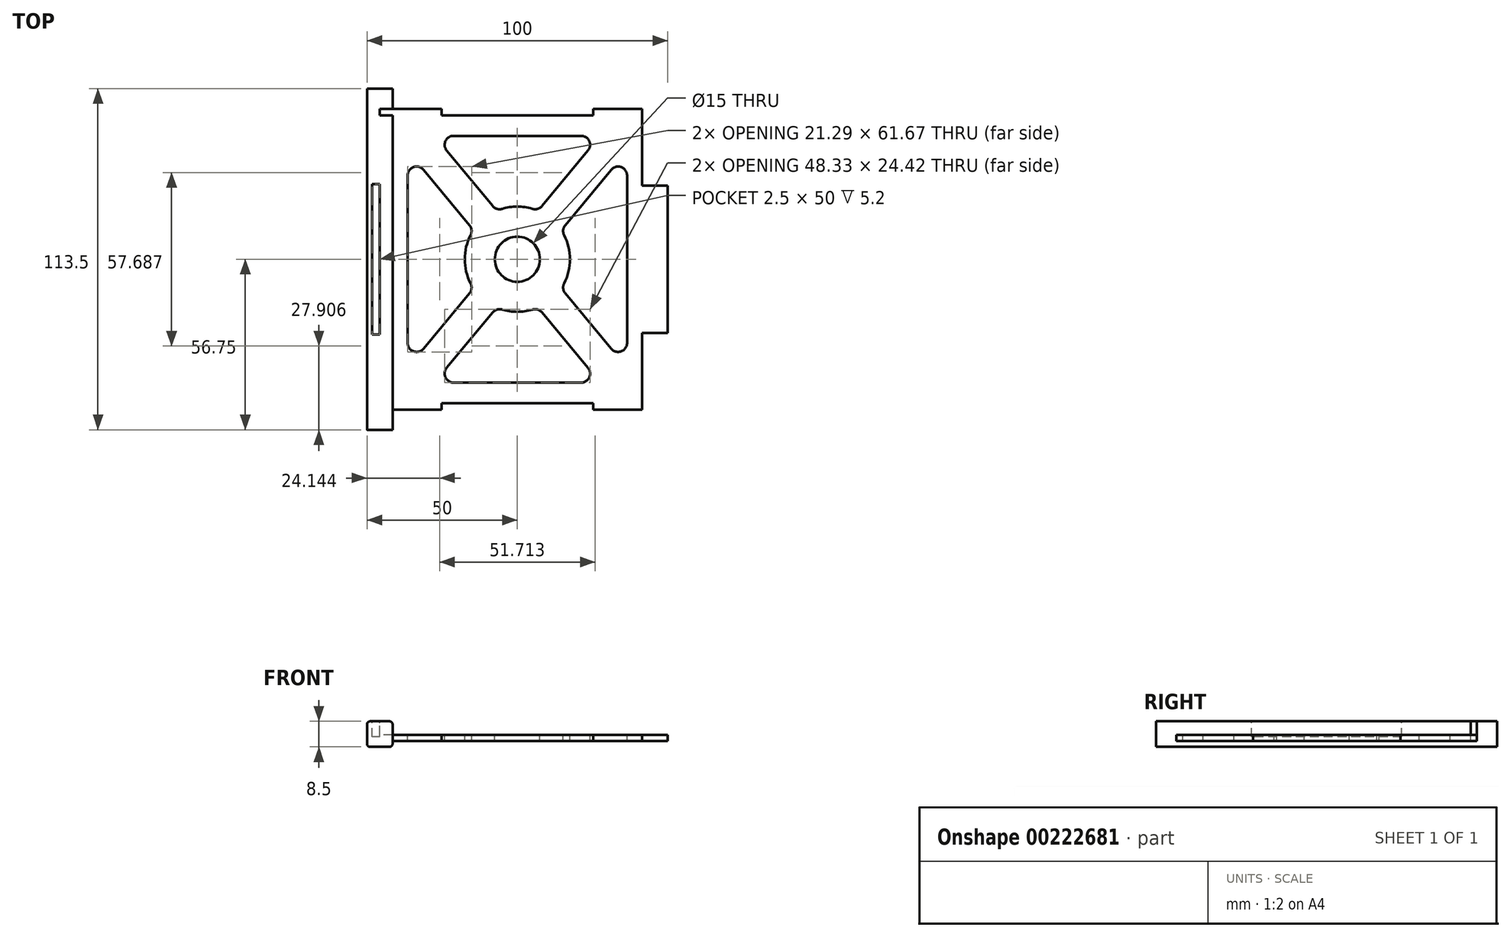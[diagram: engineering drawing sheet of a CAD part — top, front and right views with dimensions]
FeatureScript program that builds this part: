
annotation { "Feature Type Name" : "Feature", "Feature Type Description" : "" }
export const myFeature = defineFeature(function(context is Context, id is Id, definition is map)
    precondition{}
    {
        {
            var Q0;
            Q0=qCreatedBy(makeId("Top.planeOp"),FACE);
            var sketch = newSketch(context, id + "F0", { "sketchPlane" : qUnion([Q0])});
            skLineSegment(sketch, "E0.bottom", {"start": v(-50, 50) * mm, "end": v(50, 50) * mm});
            skLineSegment(sketch, "E0.top", {"start": v(-50, -50) * mm, "end": v(50, -50) * mm});
            skLineSegment(sketch, "E0.left", {"start": v(-50, 50) * mm, "end": v(-50, -50) * mm});
            skLineSegment(sketch, "E0.right", {"start": v(50, 50) * mm, "end": v(50, -50) * mm});
            skPoint(sketch, "E0.middle", {"position": v(0, 0) * mm});
            skSolve(sketch);
        }
        {
            var Q0;
            Q0=makeQuery(id+"F0.imprint","IMPRINT",FACE,{"disambiguationData":[TD([[makeQuery(id+"F0.imprint","IMPRINT",EDGE,{"derivedFrom":sQuery(id+"F0.wireOp",EDGE,"E0.bottom")}),-1.0]])]});
            extrude(context, id + "F1", {"entities" : qUnion([Q0]), "depth" : 2 * mm});
        }
        {
            var Q0;
            Q0=makeQuery(id+"F1.opExtrude","CAP_FACE",FACE,{"disambiguationData":[OSD([sQuery(id+"F0.wireOp",EDGE,"E0.bottom"),sQuery(id+"F0.wireOp",EDGE,"E0.top"),sQuery(id+"F0.wireOp",EDGE,"E0.left"),sQuery(id+"F0.wireOp",EDGE,"E0.right")])],"isStart":false});
            var sketch = newSketch(context, id + "F2", { "sketchPlane" : qUnion([Q0])});
            skCircle(sketch, "E1", {"center": v(0, 0) * mm, "radius": 7.5 * mm});
            skArc(sketch, "E2", {"start": v(-15.55, 8.04) * mm, "mid": v(-17.5, 0) * mm, "end": v(-15.55, -8.04) * mm});
            skLineSegment(sketch, "E3", {"start": v(41.5, 50) * mm, "end": v(0, 0) * mm, "construction": true});
            skLineSegment(sketch, "E4", {"start": v(-41.5, 50) * mm, "end": v(0, 0) * mm, "construction": true});
            skLineSegment(sketch, "E5", {"start": v(0, 0) * mm, "end": v(-41.5, -50) * mm, "construction": true});
            skLineSegment(sketch, "E6", {"start": v(0, 0) * mm, "end": v(41.5, -50) * mm, "construction": true});
            skLineSegment(sketch, "E7", {"start": v(-23.5, 36.14) * mm, "end": v(-8.2, 17.72) * mm});
            skLineSegment(sketch, "E8", {"start": v(-31.2, 29.75) * mm, "end": v(-15.9, 11.33) * mm});
            skLineSegment(sketch, "E9", {"start": v(-36.5, 27.84) * mm, "end": v(-36.5, -27.84) * mm});
            skLineSegment(sketch, "E10", {"start": v(-31.2, -29.75) * mm, "end": v(-15.9, -11.33) * mm});
            skLineSegment(sketch, "E11", {"start": v(-21.19, 41.05) * mm, "end": v(21.19, 41.05) * mm});
            skLineSegment(sketch, "E12", {"start": v(23.5, 36.14) * mm, "end": v(8.2, 17.72) * mm});
            skLineSegment(sketch, "E13", {"start": v(0, 50) * mm, "end": v(0, -50) * mm, "construction": true});
            skLineSegment(sketch, "E14", {"start": v(-41.5, 0) * mm, "end": v(41.5, 0) * mm, "construction": true});
            skLineSegment(sketch, "E15.MirrorCS", {"start": v(31.2, -29.75) * mm, "end": v(15.9, -11.33) * mm});
            skLineSegment(sketch, "E16.MirrorCS", {"start": v(31.2, 29.75) * mm, "end": v(15.9, 11.33) * mm});
            skLineSegment(sketch, "E17.MirrorCS", {"start": v(36.5, 27.84) * mm, "end": v(36.5, -27.84) * mm});
            skLineSegment(sketch, "E18.MirrorCS", {"start": v(23.5, -36.14) * mm, "end": v(8.2, -17.72) * mm});
            skLineSegment(sketch, "E19.MirrorCS", {"start": v(-23.5, -36.14) * mm, "end": v(-8.2, -17.72) * mm});
            skLineSegment(sketch, "E20.MirrorCS", {"start": v(-21.19, -41.05) * mm, "end": v(21.19, -41.05) * mm});
            skArc(sketch, "E21.trimOffspring", {"start": v(5.04, 16.76) * mm, "mid": v(0, 17.5) * mm, "end": v(-5.04, 16.76) * mm});
            skArc(sketch, "E22.trimOffspring", {"start": v(15.55, -8.04) * mm, "mid": v(17.5, 0) * mm, "end": v(15.55, 8.04) * mm});
            skArc(sketch, "E23.trimOffspring", {"start": v(-5.04, -16.76) * mm, "mid": v(0, -17.5) * mm, "end": v(5.04, -16.76) * mm});
            skPoint(sketch, "E24.visualSharp", {"position": v(-27.58, 41.05) * mm});
            skArc(sketch, "E24.filletArc", {"start": v(-21.19, 41.05) * mm, "mid": v(-23.9, 39.33) * mm, "end": v(-23.5, 36.14) * mm});
            skPoint(sketch, "E25.visualSharp", {"position": v(27.58, 41.05) * mm});
            skArc(sketch, "E25.filletArc", {"start": v(23.5, 36.14) * mm, "mid": v(23.9, 39.33) * mm, "end": v(21.19, 41.05) * mm});
            skPoint(sketch, "E26.visualSharp", {"position": v(6.86, 16.1) * mm});
            skArc(sketch, "E26.filletArc", {"start": v(5.04, 16.76) * mm, "mid": v(6.77, 16.76) * mm, "end": v(8.2, 17.72) * mm});
            skPoint(sketch, "E27.visualSharp", {"position": v(-6.86, 16.1) * mm});
            skArc(sketch, "E27.filletArc", {"start": v(-8.2, 17.72) * mm, "mid": v(-6.77, 16.76) * mm, "end": v(-5.04, 16.76) * mm});
            skPoint(sketch, "E28.visualSharp", {"position": v(-14.56, 9.71) * mm});
            skArc(sketch, "E28.filletArc", {"start": v(-15.55, 8.04) * mm, "mid": v(-15.23, 9.74) * mm, "end": v(-15.9, 11.33) * mm});
            skPoint(sketch, "E29.visualSharp", {"position": v(-36.5, 36.15) * mm});
            skArc(sketch, "E29.filletArc", {"start": v(-31.2, 29.75) * mm, "mid": v(-34.52, 30.66) * mm, "end": v(-36.5, 27.84) * mm});
            skPoint(sketch, "E30.visualSharp", {"position": v(-36.5, -36.15) * mm});
            skArc(sketch, "E30.filletArc", {"start": v(-36.5, -27.84) * mm, "mid": v(-34.52, -30.66) * mm, "end": v(-31.2, -29.75) * mm});
            skPoint(sketch, "E31.visualSharp", {"position": v(-14.56, -9.71) * mm});
            skArc(sketch, "E31.filletArc", {"start": v(-15.9, -11.33) * mm, "mid": v(-15.23, -9.74) * mm, "end": v(-15.55, -8.04) * mm});
            skPoint(sketch, "E32.visualSharp", {"position": v(14.56, 9.71) * mm});
            skArc(sketch, "E32.filletArc", {"start": v(15.9, 11.33) * mm, "mid": v(15.23, 9.74) * mm, "end": v(15.55, 8.04) * mm});
            skPoint(sketch, "E33.visualSharp", {"position": v(14.56, -9.71) * mm});
            skArc(sketch, "E33.filletArc", {"start": v(15.55, -8.04) * mm, "mid": v(15.23, -9.74) * mm, "end": v(15.9, -11.33) * mm});
            skPoint(sketch, "E34.visualSharp", {"position": v(6.86, -16.1) * mm});
            skArc(sketch, "E34.filletArc", {"start": v(8.2, -17.72) * mm, "mid": v(6.77, -16.76) * mm, "end": v(5.04, -16.76) * mm});
            skPoint(sketch, "E35.visualSharp", {"position": v(-6.86, -16.1) * mm});
            skArc(sketch, "E35.filletArc", {"start": v(-5.04, -16.76) * mm, "mid": v(-6.77, -16.76) * mm, "end": v(-8.2, -17.72) * mm});
            skPoint(sketch, "E36.visualSharp", {"position": v(-27.58, -41.05) * mm});
            skArc(sketch, "E36.filletArc", {"start": v(-23.5, -36.14) * mm, "mid": v(-23.9, -39.33) * mm, "end": v(-21.19, -41.05) * mm});
            skPoint(sketch, "E37.visualSharp", {"position": v(27.58, -41.05) * mm});
            skArc(sketch, "E37.filletArc", {"start": v(21.19, -41.05) * mm, "mid": v(23.9, -39.33) * mm, "end": v(23.5, -36.14) * mm});
            skPoint(sketch, "E38.visualSharp", {"position": v(36.5, -36.15) * mm});
            skArc(sketch, "E38.filletArc", {"start": v(31.2, -29.75) * mm, "mid": v(34.52, -30.66) * mm, "end": v(36.5, -27.84) * mm});
            skPoint(sketch, "E39.visualSharp", {"position": v(36.5, 36.15) * mm});
            skArc(sketch, "E39.filletArc", {"start": v(36.5, 27.84) * mm, "mid": v(34.52, 30.66) * mm, "end": v(31.2, 29.75) * mm});
            skLineSegment(sketch, "E40", {"start": v(41.5, 50) * mm, "end": v(41.5, -50) * mm, "construction": true});
            skLineSegment(sketch, "E41", {"start": v(-41.5, -50) * mm, "end": v(-41.5, 50) * mm, "construction": true});
            skLineSegment(sketch, "E42.bottom", {"start": v(-25.25, 50) * mm, "end": v(25.25, 50) * mm});
            skLineSegment(sketch, "E42.top", {"start": v(-25.25, 47.9) * mm, "end": v(25.25, 47.9) * mm});
            skLineSegment(sketch, "E42.left", {"start": v(-25.25, 50) * mm, "end": v(-25.25, 47.9) * mm});
            skLineSegment(sketch, "E42.right", {"start": v(25.25, 50) * mm, "end": v(25.25, 47.9) * mm});
            skLineSegment(sketch, "E43.MirrorCS", {"start": v(25.25, -50) * mm, "end": v(25.25, -47.9) * mm});
            skLineSegment(sketch, "E44.MirrorCS", {"start": v(-25.25, -50) * mm, "end": v(-25.25, -47.9) * mm});
            skLineSegment(sketch, "E45.MirrorCS", {"start": v(-25.25, -50) * mm, "end": v(25.25, -50) * mm});
            skLineSegment(sketch, "E46.MirrorCS", {"start": v(-25.25, -47.9) * mm, "end": v(25.25, -47.9) * mm});
            skSolve(sketch);
        }
        {
            var Q0;
            Q0=makeQuery(id+"F2.imprint","IMPRINT",FACE,{"disambiguationData":[TD([[makeQuery(id+"F2.imprint","IMPRINT",EDGE,{"derivedFrom":sQuery(id+"F2.wireOp",EDGE,"E7")}),1.0]])]});
            var Q1;
            Q1=makeQuery(id+"F2.imprint","IMPRINT",FACE,{"disambiguationData":[TD([[makeQuery(id+"F2.imprint","IMPRINT",EDGE,{"derivedFrom":sQuery(id+"F2.wireOp",EDGE,"E2")}),-1.0]])]});
            var Q2;
            Q2=makeQuery(id+"F2.imprint","IMPRINT",FACE,{"disambiguationData":[TD([[makeQuery(id+"F2.imprint","IMPRINT",EDGE,{"derivedFrom":sQuery(id+"F2.wireOp",EDGE,"E1")}),1.0]])]});
            var Q3;
            Q3=makeQuery(id+"F2.imprint","IMPRINT",FACE,{"disambiguationData":[TD([[makeQuery(id+"F2.imprint","IMPRINT",EDGE,{"derivedFrom":sQuery(id+"F2.wireOp",EDGE,"E15.MirrorCS")}),-1.0]])]});
            var Q4;
            Q4=makeQuery(id+"F2.imprint","IMPRINT",FACE,{"disambiguationData":[TD([[makeQuery(id+"F2.imprint","IMPRINT",EDGE,{"derivedFrom":sQuery(id+"F2.wireOp",EDGE,"E18.MirrorCS")}),1.0]])]});
            var Q5;
            Q5=makeQuery(id+"F2.imprint","IMPRINT",FACE,{"disambiguationData":[TD([[makeQuery(id+"F2.imprint","IMPRINT",EDGE,{"derivedFrom":sQuery(id+"F2.wireOp",EDGE,"E42.bottom")}),-1.0]])]});
            var Q6;
            Q6=makeQuery(id+"F2.imprint","IMPRINT",FACE,{"disambiguationData":[TD([[makeQuery(id+"F2.imprint","IMPRINT",EDGE,{"derivedFrom":sQuery(id+"F2.wireOp",EDGE,"E43.MirrorCS")}),1.0]])]});
            extrude(context, id + "F3", {"entities" : qUnion([Q0, Q1, Q2, Q3, Q4, Q5, Q6]), "operationType" : NewBodyOperationType.REMOVE, "oppositeDirection" : true, "depth" : 25 * mm});
        }
        {
            var Q0;
            Q0=makeQuery(id+"F1.opExtrude","CAP_FACE",FACE,{"disambiguationData":[OSD([sQuery(id+"F0.wireOp",EDGE,"E0.bottom"),sQuery(id+"F0.wireOp",EDGE,"E0.top"),sQuery(id+"F0.wireOp",EDGE,"E0.left"),sQuery(id+"F0.wireOp",EDGE,"E0.right")])],"isStart":true});
            var sketch = newSketch(context, id + "F4", { "sketchPlane" : qUnion([Q0])});
            skLineSegment(sketch, "E47.bottom", {"start": v(-50, 50) * mm, "end": v(-41.5, 50) * mm});
            skLineSegment(sketch, "E47.top", {"start": v(-50, -50) * mm, "end": v(-41.5, -50) * mm});
            skLineSegment(sketch, "E47.left", {"start": v(-50, 50) * mm, "end": v(-50, -50) * mm});
            skLineSegment(sketch, "E47.right", {"start": v(-41.5, 50) * mm, "end": v(-41.5, -50) * mm});
            skLineSegment(sketch, "E48.bottom", {"start": v(50, 50) * mm, "end": v(41.5, 50) * mm});
            skLineSegment(sketch, "E48.top", {"start": v(50, 24.5) * mm, "end": v(41.5, 24.5) * mm});
            skLineSegment(sketch, "E48.left", {"start": v(50, 50) * mm, "end": v(50, 24.5) * mm});
            skLineSegment(sketch, "E48.right", {"start": v(41.5, 50) * mm, "end": v(41.5, 24.5) * mm});
            skLineSegment(sketch, "E49.bottom", {"start": v(50, -50) * mm, "end": v(41.5, -50) * mm});
            skLineSegment(sketch, "E49.top", {"start": v(50, -24.5) * mm, "end": v(41.5, -24.5) * mm});
            skLineSegment(sketch, "E49.left", {"start": v(50, -50) * mm, "end": v(50, -24.5) * mm});
            skLineSegment(sketch, "E49.right", {"start": v(41.5, -50) * mm, "end": v(41.5, -24.5) * mm});
            skLineSegment(sketch, "E50.bottom", {"start": v(50, -24.5) * mm, "end": v(46.5, -24.5) * mm});
            skLineSegment(sketch, "E50.top", {"start": v(50, 24.5) * mm, "end": v(46.5, 24.5) * mm});
            skLineSegment(sketch, "E50.left", {"start": v(50, -24.5) * mm, "end": v(50, 24.5) * mm});
            skLineSegment(sketch, "E50.right", {"start": v(46.5, -24.5) * mm, "end": v(46.5, 24.5) * mm});
            skSolve(sketch);
        }
        {
            var Q0;
            Q0=makeQuery(id+"F4.imprint","IMPRINT",FACE,{"disambiguationData":[TD([[makeQuery(id+"F4.imprint","IMPRINT",EDGE,{"derivedFrom":sQuery(id+"F4.wireOp",EDGE,"E47.bottom")}),-1.0]])]});
            var Q1;
            Q1=makeQuery(id+"F4.imprint","IMPRINT",FACE,{"disambiguationData":[TD([[makeQuery(id+"F4.imprint","IMPRINT",EDGE,{"derivedFrom":sQuery(id+"F4.wireOp",EDGE,"E48.bottom")}),-1.0]])]});
            var Q2;
            Q2=makeQuery(id+"F4.imprint","IMPRINT",FACE,{"disambiguationData":[TD([[makeQuery(id+"F4.imprint","IMPRINT",EDGE,{"derivedFrom":sQuery(id+"F4.wireOp",EDGE,"E50.bottom")}),-1.0]])]});
            var Q3;
            Q3=makeQuery(id+"F4.imprint","IMPRINT",FACE,{"disambiguationData":[TD([[makeQuery(id+"F4.imprint","IMPRINT",EDGE,{"derivedFrom":sQuery(id+"F4.wireOp",EDGE,"E49.bottom")}),1.0]])]});
            extrude(context, id + "F5", {"entities" : qUnion([Q0, Q1, Q2, Q3]), "operationType" : NewBodyOperationType.REMOVE, "oppositeDirection" : true, "depth" : 25 * mm});
        }
        {
            var Q0;
            Q0=qCreatedBy(makeId("Front.planeOp"),FACE);
            var sketch = newSketch(context, id + "F6", { "sketchPlane" : qUnion([Q0])});
            skLineSegment(sketch, "E51.bottom", {"start": v(-41.5, -2) * mm, "end": v(-50, -2) * mm});
            skLineSegment(sketch, "E51.top", {"start": v(-41.5, 6.5) * mm, "end": v(-50, 6.5) * mm});
            skLineSegment(sketch, "E51.left", {"start": v(-41.5, -2) * mm, "end": v(-41.5, 6.5) * mm});
            skLineSegment(sketch, "E51.right", {"start": v(-50, -2) * mm, "end": v(-50, 6.5) * mm});
            skSolve(sketch);
        }
        {
            var Q0;
            Q0=makeQuery(id+"F6.imprint","IMPRINT",FACE,{"disambiguationData":[TD([[makeQuery(id+"F6.imprint","IMPRINT",EDGE,{"derivedFrom":sQuery(id+"F6.wireOp",EDGE,"E51.bottom")}),-1.0]])]});
            extrude(context, id + "F7", {"entities" : qUnion([Q0]), "operationType" : NewBodyOperationType.ADD, "endBound" : BoundingType.SYMMETRIC, "depth" : 113.5 * mm});
        }
        {
            var Q0;
            Q0=makeQuery(id+"F7.opExtrude","SWEPT_FACE",FACE,{"disambiguationData":[OSD([sQuery(id+"F6.wireOp",EDGE,"E51.top")])]});
            var sketch = newSketch(context, id + "F8", { "sketchPlane" : qUnion([Q0])});
            skLineSegment(sketch, "E52", {"start": v(-45.75, 56.75) * mm, "end": v(-45.75, -56.75) * mm, "construction": true});
            skLineSegment(sketch, "E53.bottom", {"start": v(-45.78, 25) * mm, "end": v(-48.28, 25) * mm});
            skLineSegment(sketch, "E53.top", {"start": v(-45.78, -25) * mm, "end": v(-48.28, -25) * mm});
            skLineSegment(sketch, "E53.left", {"start": v(-45.78, 25) * mm, "end": v(-45.78, -25) * mm});
            skLineSegment(sketch, "E53.right", {"start": v(-48.28, 25) * mm, "end": v(-48.28, -25) * mm});
            skSolve(sketch);
        }
        {
            var Q0;
            Q0=makeQuery(id+"F8.imprint","IMPRINT",FACE,{"disambiguationData":[TD([[makeQuery(id+"F8.imprint","IMPRINT",EDGE,{"derivedFrom":sQuery(id+"F8.wireOp",EDGE,"E53.bottom")}),1.0]])]});
            extrude(context, id + "F9", {"entities" : qUnion([Q0]), "operationType" : NewBodyOperationType.REMOVE, "oppositeDirection" : true, "depth" : 5.2 * mm});
        }
        {
            var Q0;
            Q0=makeQuery(id+"F7.opExtrude","SWEPT_EDGE",EDGE,{"disambiguationData":[OSD([sQuery(id+"F6.wireOp",EDGE,"E51.bottom"),sQuery(id+"F6.wireOp",EDGE,"E51.left")])]});
            var Q1;
            Q1=makeQuery(id+"F7.opExtrude","SWEPT_EDGE",EDGE,{"disambiguationData":[OSD([sQuery(id+"F6.wireOp",EDGE,"E51.top"),sQuery(id+"F6.wireOp",EDGE,"E51.left")])]});
            var Q2;
            Q2=makeQuery(id+"F7.opExtrude","SWEPT_EDGE",EDGE,{"disambiguationData":[OSD([sQuery(id+"F6.wireOp",EDGE,"E51.bottom"),sQuery(id+"F6.wireOp",EDGE,"E51.right")])]});
            var Q3;
            Q3=makeQuery(id+"F7.opExtrude","SWEPT_EDGE",EDGE,{"disambiguationData":[OSD([sQuery(id+"F6.wireOp",EDGE,"E51.top"),sQuery(id+"F6.wireOp",EDGE,"E51.right")])]});
            fillet(context, id + "F10", {"entities" : qUnion([Q0, Q1, Q2, Q3]), "radius" : 1 * mm, "tangentPropagation" : true, "allowEdgeOverflow" : false});
        }
        {
            var Q0;
            Q0=makeQuery(id+"F7.opExtrude","SWEPT_FACE",FACE,{"disambiguationData":[OSD([sQuery(id+"F6.wireOp",EDGE,"E51.top")])]});
            var sketch = newSketch(context, id + "F11", { "sketchPlane" : qUnion([Q0])});
            skLineSegment(sketch, "E54.bottom", {"start": v(-45.83, 50) * mm, "end": v(-41.5, 50) * mm});
            skLineSegment(sketch, "E54.top", {"start": v(-45.83, 47.9) * mm, "end": v(-41.5, 47.9) * mm});
            skLineSegment(sketch, "E54.left", {"start": v(-45.83, 50) * mm, "end": v(-45.83, 47.9) * mm});
            skLineSegment(sketch, "E54.right", {"start": v(-41.5, 50) * mm, "end": v(-41.5, 47.9) * mm});
            skSolve(sketch);
        }
        {
            var Q0;
            {var subQ0=sQuery(id+"F11.wireOp",EDGE,"E54.right");Q0=makeQuery(id+"F11.imprint","IMPRINT",FACE,{"disambiguationData":[TD([[makeQuery(id+"F11.imprint","IMPRINT",EDGE,{"derivedFrom":subQ0}),-1.0]])]});}
            var Q1;
            {var subQ0=sQuery(id+"F11.wireOp",EDGE,"E54.left");Q1=makeQuery(id+"F11.imprint","IMPRINT",FACE,{"disambiguationData":[TD([[makeQuery(id+"F11.imprint","IMPRINT",EDGE,{"derivedFrom":subQ0}),1.0]])]});}
            var Q2;
            Q2=makeQuery(id+"F1.opExtrude","CAP_FACE",FACE,{"disambiguationData":[OSD([sQuery(id+"F0.wireOp",EDGE,"E0.bottom"),sQuery(id+"F0.wireOp",EDGE,"E0.top"),sQuery(id+"F0.wireOp",EDGE,"E0.left"),sQuery(id+"F0.wireOp",EDGE,"E0.right")])],"isStart":false});
            extrude(context, id + "F12", {"entities" : qUnion([Q0, Q1]), "operationType" : NewBodyOperationType.REMOVE, "endBound" : BoundingType.UP_TO_SURFACE, "oppositeDirection" : true, "endBoundEntityFace" : qUnion([Q2]), "depth" : 25 * mm});
        }
    });
